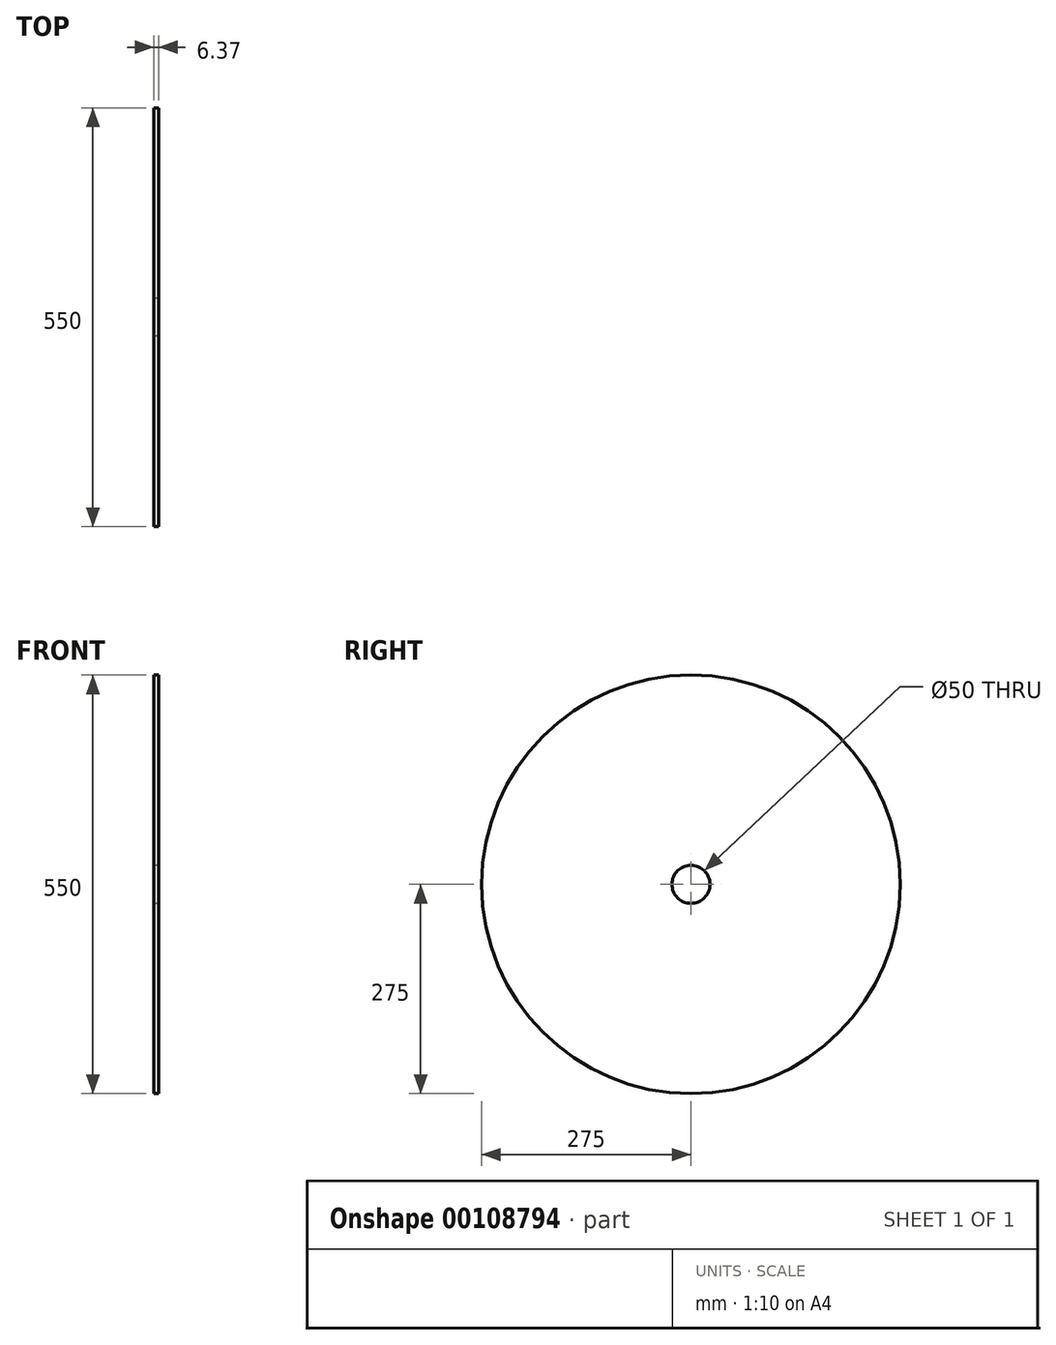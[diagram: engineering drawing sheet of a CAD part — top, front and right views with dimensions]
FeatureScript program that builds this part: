
annotation { "Feature Type Name" : "Feature", "Feature Type Description" : "" }
export const myFeature = defineFeature(function(context is Context, id is Id, definition is map)
    precondition{}
    {
        {
            var Q0;
            Q0=qCreatedBy(makeId("Front.planeOp"),FACE);
            var sketch = newSketch(context, id + "F0", { "sketchPlane" : qUnion([Q0])});
            skLineSegment(sketch, "E0", {"start": v(0, 25) * mm, "end": v(0, 275) * mm});
            skLineSegment(sketch, "E1", {"start": v(0, 275) * mm, "end": v(6.37, 275) * mm});
            skLineSegment(sketch, "E2", {"start": v(6.37, 275) * mm, "end": v(6.37, 25) * mm});
            skLineSegment(sketch, "E3", {"start": v(6.37, 25) * mm, "end": v(0, 25) * mm});
            skLineSegment(sketch, "E4", {"start": v(-215.6, 0) * mm, "end": v(244.9, 0) * mm, "construction": true});
            skLineSegment(sketch, "E5", {"start": v(6.37, 25) * mm, "end": v(6.37, 0) * mm});
            skLineSegment(sketch, "E6", {"start": v(6.37, 0) * mm, "end": v(0, 0) * mm});
            skLineSegment(sketch, "E7", {"start": v(0, 0) * mm, "end": v(0, 25) * mm});
            skLineSegment(sketch, "E8", {"start": v(6.37, 275) * mm, "end": v(15.65, 275) * mm});
            skLineSegment(sketch, "E9", {"start": v(15.65, 275) * mm, "end": v(14.65, 272.48) * mm});
            skSolve(sketch);
        }
        {
            var Q0;
            Q0=makeQuery(id+"F0.imprint","IMPRINT",FACE,{"disambiguationData":[TD([[makeQuery(id+"F0.imprint","IMPRINT",EDGE,{"derivedFrom":sQuery(id+"F0.wireOp",EDGE,"E0")}),-1.0]])]});
            var Q1;
            Q1=sQuery(id+"F0.wireOp",EDGE,"E4");
            revolve(context, id + "F1", {"entities" : qUnion([Q0]), "axis" : qUnion([Q1]), "revolveType" : RevolveType.FULL});
        }
    });
